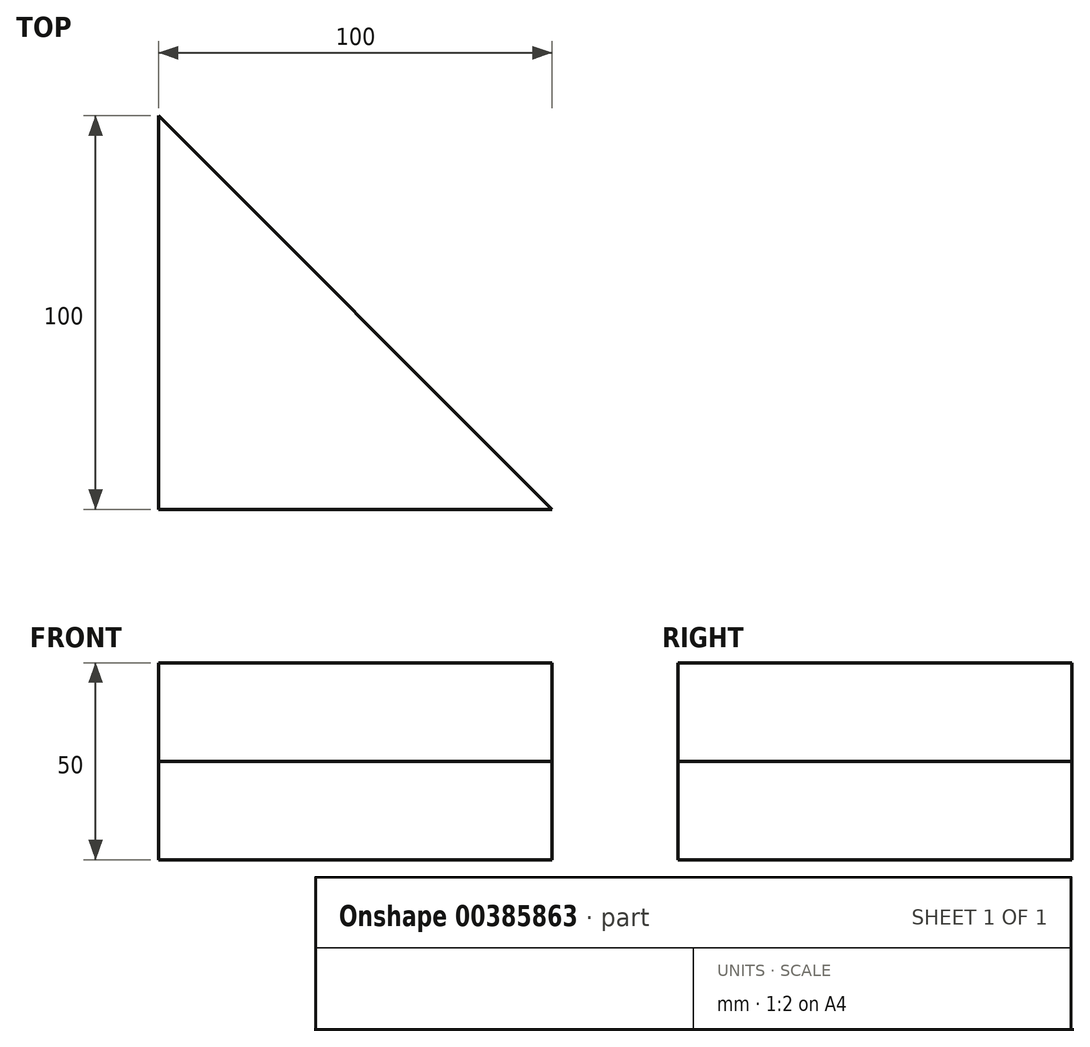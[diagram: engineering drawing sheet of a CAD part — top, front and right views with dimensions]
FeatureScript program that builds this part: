
annotation { "Feature Type Name" : "Feature", "Feature Type Description" : "" }
export const myFeature = defineFeature(function(context is Context, id is Id, definition is map)
    precondition{}
    {
        {
            var Q0;
            Q0=qCreatedBy(makeId("Top.planeOp"),FACE);
            var sketch = newSketch(context, id + "F0", { "sketchPlane" : qUnion([Q0])});
            skLineSegment(sketch, "E0", {"start": v(0, 0) * mm, "end": v(100, 0) * mm});
            skLineSegment(sketch, "E1", {"start": v(100, 0) * mm, "end": v(0, 100) * mm});
            skLineSegment(sketch, "E2", {"start": v(0, 100) * mm, "end": v(0, 0) * mm});
            skSolve(sketch);
        }
        {
            var Q0;
            Q0 = qSketchRegion(id + "F0", true);
            extrude(context, id + "F1", {"entities" : qUnion([Q0]), "depth" : 25 * mm});
        }
        {
            var Q0;
            Q0=makeQuery(id+"F1.opExtrude","SWEPT_BODY",BODY,{"disambiguationData":[OSD([sQuery(id+"F0.wireOp",EDGE,"E0"),sQuery(id+"F0.wireOp",EDGE,"E1"),sQuery(id+"F0.wireOp",EDGE,"E2")])]});
            transform(context, id + "F2", {"entities" : qUnion([Q0]), "transformType" : TransformType.TRANSLATION_3D, "dx" : 0 * mm, "dy" : 0 * mm, "dz" : 25 * mm, "makeCopy" : true});
        }
    });
